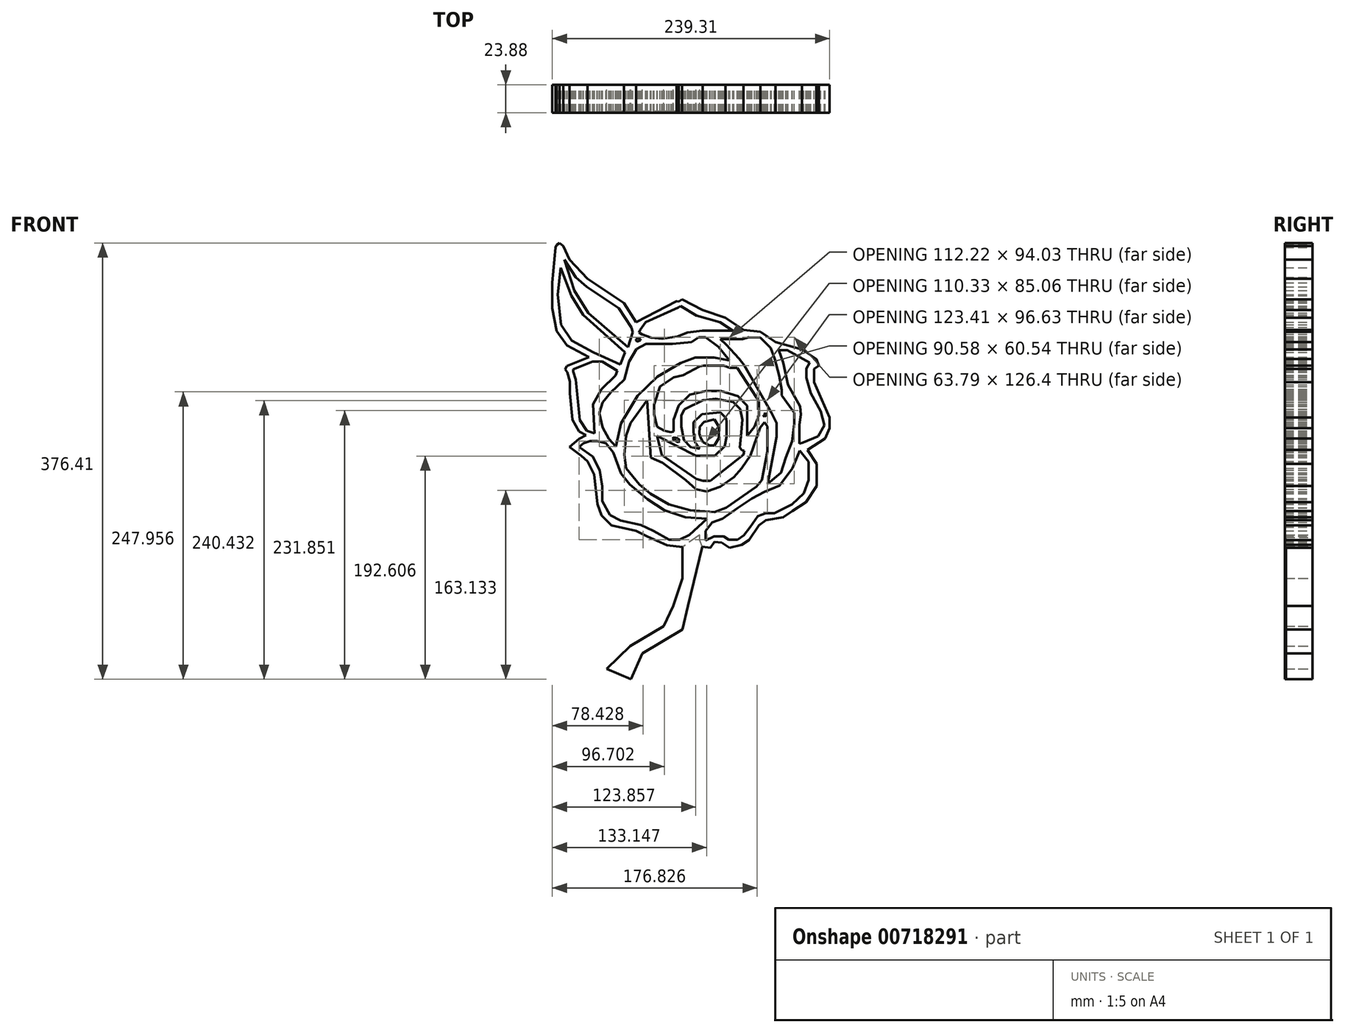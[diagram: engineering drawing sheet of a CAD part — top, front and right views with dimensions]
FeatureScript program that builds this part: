
annotation { "Feature Type Name" : "Feature", "Feature Type Description" : "" }
export const myFeature = defineFeature(function(context is Context, id is Id, definition is map)
    precondition{}
    {
        {
            var Q0;
            Q0=qCreatedBy(makeId("Front.planeOp"),FACE);
            var sketch = newSketch(context, id + "F0", { "sketchPlane" : qUnion([Q0])});
            skLineSegment(sketch, "E0", {"start": v(-232.05, 241.43) * mm, "end": v(-222.86, 217.3) * mm});
            skLineSegment(sketch, "E1", {"start": v(-222.86, 217.3) * mm, "end": v(-212.75, 200.98) * mm});
            skLineSegment(sketch, "E2", {"start": v(-212.75, 200.98) * mm, "end": v(-176.66, 168.58) * mm});
            skLineSegment(sketch, "E3", {"start": v(-176.66, 168.58) * mm, "end": v(-180.8, 158) * mm});
            skLineSegment(sketch, "E4", {"start": v(-180.8, 158) * mm, "end": v(-203.78, 168.58) * mm});
            skLineSegment(sketch, "E5", {"start": v(-203.78, 168.58) * mm, "end": v(-222.4, 178.69) * mm});
            skLineSegment(sketch, "E6", {"start": v(-222.4, 178.69) * mm, "end": v(-231.82, 192.25) * mm});
            skLineSegment(sketch, "E7", {"start": v(-231.82, 192.25) * mm, "end": v(-234.58, 218.45) * mm});
            skLineSegment(sketch, "E8", {"start": v(-234.58, 218.45) * mm, "end": v(-232.05, 241.43) * mm});
            skLineSegment(sketch, "E9", {"start": v(-228.84, 248.56) * mm, "end": v(-220.33, 221.67) * mm});
            skLineSegment(sketch, "E10", {"start": v(-220.33, 221.67) * mm, "end": v(-208.38, 202.36) * mm});
            skLineSegment(sketch, "E11", {"start": v(-208.38, 202.36) * mm, "end": v(-173.9, 172.94) * mm});
            skLineSegment(sketch, "E12", {"start": v(-173.9, 172.94) * mm, "end": v(-169.76, 185.81) * mm});
            skLineSegment(sketch, "E13", {"start": v(-169.76, 185.81) * mm, "end": v(-171.27, 190.12) * mm});
            skLineSegment(sketch, "E14", {"start": v(-171.27, 190.12) * mm, "end": v(-181.94, 206.5) * mm});
            skLineSegment(sketch, "E15", {"start": v(-181.94, 206.5) * mm, "end": v(-209.53, 225.11) * mm});
            skLineSegment(sketch, "E16", {"start": v(-209.53, 225.11) * mm, "end": v(-218.95, 233.39) * mm});
            skLineSegment(sketch, "E17", {"start": v(-218.95, 233.39) * mm, "end": v(-228.84, 248.56) * mm});
            skLineSegment(sketch, "E18", {"start": v(-221.16, 152) * mm, "end": v(-218.95, 145.01) * mm});
            skLineSegment(sketch, "E19", {"start": v(-218.95, 145.01) * mm, "end": v(-215.7, 110.18) * mm});
            skLineSegment(sketch, "E20", {"start": v(-215.7, 110.18) * mm, "end": v(-209.53, 100.89) * mm});
            skLineSegment(sketch, "E21", {"start": v(-209.53, 100.89) * mm, "end": v(-202.83, 98.73) * mm});
            skLineSegment(sketch, "E22", {"start": v(-202.83, 98.73) * mm, "end": v(-204.08, 123.8) * mm});
            skLineSegment(sketch, "E23", {"start": v(-204.08, 123.8) * mm, "end": v(-196.82, 136.67) * mm});
            skLineSegment(sketch, "E24", {"start": v(-196.82, 136.67) * mm, "end": v(-184.67, 148.4) * mm});
            skLineSegment(sketch, "E25", {"start": v(-184.67, 148.4) * mm, "end": v(-183.31, 152.6) * mm});
            skLineSegment(sketch, "E26", {"start": v(-183.31, 152.6) * mm, "end": v(-196.1, 160.52) * mm});
            skLineSegment(sketch, "E27", {"start": v(-196.1, 160.52) * mm, "end": v(-204.61, 160.52) * mm});
            skLineSegment(sketch, "E28", {"start": v(-204.61, 160.52) * mm, "end": v(-221.16, 153.85) * mm});
            skLineSegment(sketch, "E29", {"start": v(-221.16, 153.85) * mm, "end": v(-221.16, 152) * mm});
            skLineSegment(sketch, "E30", {"start": v(-166.75, 171.42) * mm, "end": v(-172.92, 160.37) * mm});
            skLineSegment(sketch, "E31", {"start": v(-172.92, 160.37) * mm, "end": v(-177.15, 145.01) * mm});
            skLineSegment(sketch, "E32", {"start": v(-177.15, 145.01) * mm, "end": v(-188.85, 133.72) * mm});
            skLineSegment(sketch, "E33", {"start": v(-188.85, 133.72) * mm, "end": v(-196, 125.27) * mm});
            skLineSegment(sketch, "E34", {"start": v(-196, 125.27) * mm, "end": v(-198.72, 115.93) * mm});
            skLineSegment(sketch, "E35", {"start": v(-198.72, 115.93) * mm, "end": v(-195.82, 103.76) * mm});
            skLineSegment(sketch, "E36", {"start": v(-195.82, 103.76) * mm, "end": v(-190.6, 93.7) * mm});
            skLineSegment(sketch, "E37", {"start": v(-190.6, 93.7) * mm, "end": v(-187.1, 90.09) * mm});
            skLineSegment(sketch, "E38", {"start": v(-187.1, 90.09) * mm, "end": v(-184.44, 87.32) * mm});
            skLineSegment(sketch, "E39", {"start": v(-184.44, 87.32) * mm, "end": v(-179.97, 107.04) * mm});
            skLineSegment(sketch, "E40", {"start": v(-179.97, 107.04) * mm, "end": v(-165.86, 131) * mm});
            skLineSegment(sketch, "E41", {"start": v(-165.86, 131) * mm, "end": v(-148.63, 147.63) * mm});
            skLineSegment(sketch, "E42", {"start": v(-148.63, 147.63) * mm, "end": v(-128.71, 159.28) * mm});
            skLineSegment(sketch, "E43", {"start": v(-128.71, 159.28) * mm, "end": v(-115.83, 164.1) * mm});
            skLineSegment(sketch, "E44", {"start": v(-115.83, 164.1) * mm, "end": v(-99.62, 164.1) * mm});
            skLineSegment(sketch, "E45", {"start": v(-99.62, 164.1) * mm, "end": v(-86.5, 161.36) * mm});
            skLineSegment(sketch, "E46", {"start": v(-86.5, 161.36) * mm, "end": v(-95.92, 173.3) * mm});
            skLineSegment(sketch, "E47", {"start": v(-95.92, 173.3) * mm, "end": v(-106.96, 181.35) * mm});
            skLineSegment(sketch, "E48", {"start": v(-106.96, 181.35) * mm, "end": v(-112.93, 181.35) * mm});
            skLineSegment(sketch, "E49", {"start": v(-112.93, 181.35) * mm, "end": v(-119.14, 177.44) * mm});
            skLineSegment(sketch, "E50", {"start": v(-119.14, 177.44) * mm, "end": v(-135.69, 175.6) * mm});
            skLineSegment(sketch, "E51", {"start": v(-135.69, 175.6) * mm, "end": v(-158.45, 175.6) * mm});
            skLineSegment(sketch, "E52", {"start": v(-158.45, 175.6) * mm, "end": v(-166.75, 171.42) * mm});
            skLineSegment(sketch, "E53", {"start": v(-216.05, 86.96) * mm, "end": v(-204.56, 78.46) * mm});
            skLineSegment(sketch, "E54", {"start": v(-204.56, 78.46) * mm, "end": v(-198.35, 66.97) * mm});
            skLineSegment(sketch, "E55", {"start": v(-198.35, 66.97) * mm, "end": v(-196.05, 52.95) * mm});
            skLineSegment(sketch, "E56", {"start": v(-196.05, 52.95) * mm, "end": v(-196.05, 40.3) * mm});
            skLineSegment(sketch, "E57", {"start": v(-196.05, 40.3) * mm, "end": v(-189.62, 28.12) * mm});
            skLineSegment(sketch, "E58", {"start": v(-189.62, 28.12) * mm, "end": v(-180.42, 23.3) * mm});
            skLineSegment(sketch, "E59", {"start": v(-180.42, 23.3) * mm, "end": v(-162.95, 19.62) * mm});
            skLineSegment(sketch, "E60", {"start": v(-162.95, 19.62) * mm, "end": v(-152.15, 14.34) * mm});
            skLineSegment(sketch, "E61", {"start": v(-152.15, 14.34) * mm, "end": v(-138.36, 6.98) * mm});
            skLineSegment(sketch, "E62", {"start": v(-138.36, 6.98) * mm, "end": v(-129.4, 6.98) * mm});
            skLineSegment(sketch, "E63", {"start": v(-129.4, 6.98) * mm, "end": v(-120.89, 10.89) * mm});
            skLineSegment(sketch, "E64", {"start": v(-120.89, 10.89) * mm, "end": v(-105.71, 24.9) * mm});
            skLineSegment(sketch, "E65", {"start": v(-105.71, 24.9) * mm, "end": v(-124.4, 26.23) * mm});
            skLineSegment(sketch, "E66", {"start": v(-124.4, 26.23) * mm, "end": v(-142.6, 32.4) * mm});
            skLineSegment(sketch, "E67", {"start": v(-142.6, 32.4) * mm, "end": v(-157.24, 41.83) * mm});
            skLineSegment(sketch, "E68", {"start": v(-157.24, 41.83) * mm, "end": v(-172.35, 54.5) * mm});
            skLineSegment(sketch, "E69", {"start": v(-172.35, 54.5) * mm, "end": v(-180, 64.1) * mm});
            skLineSegment(sketch, "E70", {"start": v(-180, 64.1) * mm, "end": v(-186.66, 81.97) * mm});
            skLineSegment(sketch, "E71", {"start": v(-186.66, 81.97) * mm, "end": v(-193.16, 90.1) * mm});
            skLineSegment(sketch, "E72", {"start": v(-193.16, 90.1) * mm, "end": v(-200.63, 92.04) * mm});
            skLineSegment(sketch, "E73", {"start": v(-200.63, 92.04) * mm, "end": v(-206.65, 92.04) * mm});
            skLineSegment(sketch, "E74", {"start": v(-206.65, 92.04) * mm, "end": v(-212.34, 90.1) * mm});
            skLineSegment(sketch, "E75", {"start": v(-212.34, 90.1) * mm, "end": v(-216.05, 86.96) * mm});
            skLineSegment(sketch, "E76", {"start": v(-163.4, 187.7) * mm, "end": v(-158.81, 194.5) * mm});
            skLineSegment(sketch, "E77", {"start": v(-158.81, 194.5) * mm, "end": v(-130.56, 207.21) * mm});
            skLineSegment(sketch, "E78", {"start": v(-130.56, 207.21) * mm, "end": v(-128.72, 208.41) * mm});
            skLineSegment(sketch, "E79", {"start": v(-128.72, 208.41) * mm, "end": v(-114.94, 200.32) * mm});
            skLineSegment(sketch, "E80", {"start": v(-114.94, 200.32) * mm, "end": v(-94.45, 194.62) * mm});
            skLineSegment(sketch, "E81", {"start": v(-94.45, 194.62) * mm, "end": v(-83.52, 187.24) * mm});
            skLineSegment(sketch, "E82", {"start": v(-83.52, 187.24) * mm, "end": v(-88.47, 187.24) * mm});
            skLineSegment(sketch, "E83", {"start": v(-88.47, 187.24) * mm, "end": v(-109.85, 187.24) * mm});
            skLineSegment(sketch, "E84", {"start": v(-109.85, 187.24) * mm, "end": v(-122.51, 185.5) * mm});
            skLineSegment(sketch, "E85", {"start": v(-122.51, 185.5) * mm, "end": v(-131.4, 182.08) * mm});
            skLineSegment(sketch, "E86", {"start": v(-131.4, 182.08) * mm, "end": v(-144.44, 180.23) * mm});
            skLineSegment(sketch, "E87", {"start": v(-144.44, 180.23) * mm, "end": v(-154.1, 181.3) * mm});
            skLineSegment(sketch, "E88", {"start": v(-154.1, 181.3) * mm, "end": v(-161.93, 184) * mm});
            skLineSegment(sketch, "E89", {"start": v(-161.93, 184) * mm, "end": v(-164.44, 185.7) * mm});
            skLineSegment(sketch, "E90", {"start": v(-164.44, 185.7) * mm, "end": v(-163.4, 187.7) * mm});
            skLineSegment(sketch, "E91", {"start": v(-94.38, 179.88) * mm, "end": v(-75.05, 179.88) * mm});
            skLineSegment(sketch, "E92", {"start": v(-75.05, 179.88) * mm, "end": v(-69.83, 181.43) * mm});
            skLineSegment(sketch, "E93", {"start": v(-69.83, 181.43) * mm, "end": v(-59.58, 181.04) * mm});
            skLineSegment(sketch, "E94", {"start": v(-59.58, 181.04) * mm, "end": v(-50.89, 172.15) * mm});
            skLineSegment(sketch, "E95", {"start": v(-50.89, 172.15) * mm, "end": v(-47.4, 162.88) * mm});
            skLineSegment(sketch, "E96", {"start": v(-47.4, 162.88) * mm, "end": v(-43.35, 148.58) * mm});
            skLineSegment(sketch, "E97", {"start": v(-43.35, 148.58) * mm, "end": v(-41.22, 136.01) * mm});
            skLineSegment(sketch, "E98", {"start": v(-41.22, 136.01) * mm, "end": v(-41.22, 131.38) * mm});
            skLineSegment(sketch, "E99", {"start": v(-41.22, 131.38) * mm, "end": v(-30.6, 116.5) * mm});
            skLineSegment(sketch, "E100", {"start": v(-30.6, 116.5) * mm, "end": v(-30.6, 106.78) * mm});
            skLineSegment(sketch, "E101", {"start": v(-30.6, 106.78) * mm, "end": v(-32.47, 91.61) * mm});
            skLineSegment(sketch, "E102", {"start": v(-32.47, 91.61) * mm, "end": v(-37.66, 77.8) * mm});
            skLineSegment(sketch, "E103", {"start": v(-37.66, 77.8) * mm, "end": v(-41.99, 64.72) * mm});
            skLineSegment(sketch, "E104", {"start": v(-41.99, 64.72) * mm, "end": v(-53.2, 55.03) * mm});
            skLineSegment(sketch, "E105", {"start": v(-53.2, 55.03) * mm, "end": v(-45.57, 95.66) * mm});
            skLineSegment(sketch, "E106", {"start": v(-45.57, 95.66) * mm, "end": v(-45.57, 107.52) * mm});
            skLineSegment(sketch, "E107", {"start": v(-45.57, 107.52) * mm, "end": v(-50.12, 116.5) * mm});
            skLineSegment(sketch, "E108", {"start": v(-50.12, 116.5) * mm, "end": v(-73.68, 157.41) * mm});
            skLineSegment(sketch, "E109", {"start": v(-73.68, 157.41) * mm, "end": v(-78.17, 163.1) * mm});
            skLineSegment(sketch, "E110", {"start": v(-78.17, 163.1) * mm, "end": v(-89.3, 175) * mm});
            skLineSegment(sketch, "E111", {"start": v(-89.3, 175) * mm, "end": v(-94.38, 179.88) * mm});
            skLineSegment(sketch, "E112", {"start": v(-157.5, 127.3) * mm, "end": v(-171.82, 107.52) * mm});
            skLineSegment(sketch, "E113", {"start": v(-171.82, 107.52) * mm, "end": v(-175.65, 96.81) * mm});
            skLineSegment(sketch, "E114", {"start": v(-175.65, 96.81) * mm, "end": v(-177.16, 80.3) * mm});
            skLineSegment(sketch, "E115", {"start": v(-177.16, 80.3) * mm, "end": v(-175.65, 68.32) * mm});
            skLineSegment(sketch, "E116", {"start": v(-175.65, 68.32) * mm, "end": v(-164.1, 54.62) * mm});
            skLineSegment(sketch, "E117", {"start": v(-164.1, 54.62) * mm, "end": v(-154.46, 46.55) * mm});
            skLineSegment(sketch, "E118", {"start": v(-154.46, 46.55) * mm, "end": v(-138.8, 37.32) * mm});
            skLineSegment(sketch, "E119", {"start": v(-138.8, 37.32) * mm, "end": v(-120.4, 32.22) * mm});
            skLineSegment(sketch, "E120", {"start": v(-120.4, 32.22) * mm, "end": v(-99.3, 30.67) * mm});
            skLineSegment(sketch, "E121", {"start": v(-99.3, 30.67) * mm, "end": v(-89.3, 34.44) * mm});
            skLineSegment(sketch, "E122", {"start": v(-89.3, 34.44) * mm, "end": v(-63.17, 52.6) * mm});
            skLineSegment(sketch, "E123", {"start": v(-63.17, 52.6) * mm, "end": v(-58.4, 58.3) * mm});
            skLineSegment(sketch, "E124", {"start": v(-58.4, 58.3) * mm, "end": v(-53.75, 83.02) * mm});
            skLineSegment(sketch, "E125", {"start": v(-53.75, 83.02) * mm, "end": v(-53.75, 104.5) * mm});
            skLineSegment(sketch, "E126", {"start": v(-53.75, 104.5) * mm, "end": v(-55.51, 107.04) * mm});
            skLineSegment(sketch, "E127", {"start": v(-55.51, 107.04) * mm, "end": v(-56.2, 108.02) * mm});
            skLineSegment(sketch, "E128", {"start": v(-56.2, 108.02) * mm, "end": v(-59.88, 103.36) * mm});
            skLineSegment(sketch, "E129", {"start": v(-59.88, 103.36) * mm, "end": v(-68.22, 79.47) * mm});
            skLineSegment(sketch, "E130", {"start": v(-68.22, 79.47) * mm, "end": v(-75.9, 68.54) * mm});
            skLineSegment(sketch, "E131", {"start": v(-75.9, 68.54) * mm, "end": v(-82.4, 60.86) * mm});
            skLineSegment(sketch, "E132", {"start": v(-82.4, 60.86) * mm, "end": v(-94.27, 52.6) * mm});
            skLineSegment(sketch, "E133", {"start": v(-94.27, 52.6) * mm, "end": v(-106.03, 48.46) * mm});
            skLineSegment(sketch, "E134", {"start": v(-106.03, 48.46) * mm, "end": v(-115.37, 50.21) * mm});
            skLineSegment(sketch, "E135", {"start": v(-115.37, 50.21) * mm, "end": v(-124.05, 58.3) * mm});
            skLineSegment(sketch, "E136", {"start": v(-124.05, 58.3) * mm, "end": v(-144.13, 73.27) * mm});
            skLineSegment(sketch, "E137", {"start": v(-144.13, 73.27) * mm, "end": v(-154.17, 77.7) * mm});
            skLineSegment(sketch, "E138", {"start": v(-154.17, 77.7) * mm, "end": v(-157.5, 127.3) * mm});
            skLineSegment(sketch, "E139", {"start": v(-149, 96.54) * mm, "end": v(-115.36, 79.15) * mm});
            skLineSegment(sketch, "E140", {"start": v(-115.36, 79.15) * mm, "end": v(-99.11, 79.15) * mm});
            skLineSegment(sketch, "E141", {"start": v(-99.11, 79.15) * mm, "end": v(-90.55, 87.42) * mm});
            skLineSegment(sketch, "E142", {"start": v(-90.55, 87.42) * mm, "end": v(-88.96, 95.87) * mm});
            skLineSegment(sketch, "E143", {"start": v(-88.96, 95.87) * mm, "end": v(-88.96, 108.02) * mm});
            skLineSegment(sketch, "E144", {"start": v(-88.96, 108.02) * mm, "end": v(-89.34, 111.66) * mm});
            skLineSegment(sketch, "E145", {"start": v(-89.34, 111.66) * mm, "end": v(-94.28, 116.77) * mm});
            skLineSegment(sketch, "E146", {"start": v(-94.28, 116.77) * mm, "end": v(-110.01, 115.11) * mm});
            skLineSegment(sketch, "E147", {"start": v(-110.01, 115.11) * mm, "end": v(-117.36, 108.02) * mm});
            skLineSegment(sketch, "E148", {"start": v(-117.36, 108.02) * mm, "end": v(-117.36, 100.19) * mm});
            skLineSegment(sketch, "E149", {"start": v(-117.36, 100.19) * mm, "end": v(-116.45, 91.6) * mm});
            skLineSegment(sketch, "E150", {"start": v(-116.45, 91.6) * mm, "end": v(-112.11, 85.36) * mm});
            skLineSegment(sketch, "E151", {"start": v(-112.11, 85.36) * mm, "end": v(-119.91, 86.83) * mm});
            skLineSegment(sketch, "E152", {"start": v(-119.91, 86.83) * mm, "end": v(-125.72, 92.85) * mm});
            skLineSegment(sketch, "E153", {"start": v(-125.72, 92.85) * mm, "end": v(-127.96, 104.4) * mm});
            skLineSegment(sketch, "E154", {"start": v(-127.96, 104.4) * mm, "end": v(-127.96, 113.98) * mm});
            skLineSegment(sketch, "E155", {"start": v(-127.96, 113.98) * mm, "end": v(-125.34, 119.11) * mm});
            skLineSegment(sketch, "E156", {"start": v(-125.34, 119.11) * mm, "end": v(-109.15, 127.3) * mm});
            skLineSegment(sketch, "E157", {"start": v(-109.15, 127.3) * mm, "end": v(-98.4, 128.43) * mm});
            skLineSegment(sketch, "E158", {"start": v(-98.4, 128.43) * mm, "end": v(-90.53, 126.95) * mm});
            skLineSegment(sketch, "E159", {"start": v(-90.53, 126.95) * mm, "end": v(-83.02, 125.54) * mm});
            skLineSegment(sketch, "E160", {"start": v(-83.02, 125.54) * mm, "end": v(-77.24, 119.55) * mm});
            skLineSegment(sketch, "E161", {"start": v(-77.24, 119.55) * mm, "end": v(-75.18, 110.45) * mm});
            skLineSegment(sketch, "E162", {"start": v(-75.18, 110.45) * mm, "end": v(-76.55, 96.08) * mm});
            skLineSegment(sketch, "E163", {"start": v(-76.55, 96.08) * mm, "end": v(-77.6, 86.16) * mm});
            skLineSegment(sketch, "E164", {"start": v(-77.6, 86.16) * mm, "end": v(-75.56, 84.05) * mm});
            skLineSegment(sketch, "E165", {"start": v(-75.56, 84.05) * mm, "end": v(-73.74, 83.7) * mm});
            skLineSegment(sketch, "E166", {"start": v(-73.74, 83.7) * mm, "end": v(-74.39, 80.29) * mm});
            skLineSegment(sketch, "E167", {"start": v(-74.39, 80.29) * mm, "end": v(-102.9, 57.7) * mm});
            skLineSegment(sketch, "E168", {"start": v(-102.9, 57.7) * mm, "end": v(-109.24, 57.7) * mm});
            skLineSegment(sketch, "E169", {"start": v(-109.24, 57.7) * mm, "end": v(-115, 59.28) * mm});
            skLineSegment(sketch, "E170", {"start": v(-115, 59.28) * mm, "end": v(-144.74, 79.9) * mm});
            skLineSegment(sketch, "E171", {"start": v(-144.74, 79.9) * mm, "end": v(-149, 96.54) * mm});
            skLineSegment(sketch, "E172", {"start": v(-70.97, 96.54) * mm, "end": v(-70.97, 122.54) * mm});
            skPoint(sketch, "E172.endSnap0", {"position": v(-80.13, 122.54) * mm});
            skLineSegment(sketch, "E173", {"start": v(-70.97, 122.54) * mm, "end": v(-78.94, 130.8) * mm});
            skLineSegment(sketch, "E174", {"start": v(-78.94, 130.8) * mm, "end": v(-93.58, 135.23) * mm});
            skLineSegment(sketch, "E175", {"start": v(-93.58, 135.23) * mm, "end": v(-106.66, 135.23) * mm});
            skLineSegment(sketch, "E176", {"start": v(-106.66, 135.23) * mm, "end": v(-120.6, 132.07) * mm});
            skLineSegment(sketch, "E177", {"start": v(-120.6, 132.07) * mm, "end": v(-130.28, 122.73) * mm});
            skLineSegment(sketch, "E178", {"start": v(-130.28, 122.73) * mm, "end": v(-134.62, 110.45) * mm});
            skLineSegment(sketch, "E179", {"start": v(-134.62, 110.45) * mm, "end": v(-134.62, 100.19) * mm});
            skLineSegment(sketch, "E180", {"start": v(-134.62, 100.19) * mm, "end": v(-136.78, 99.7) * mm});
            skLineSegment(sketch, "E181", {"start": v(-136.78, 99.7) * mm, "end": v(-142.5, 100.78) * mm});
            skLineSegment(sketch, "E182", {"start": v(-142.5, 100.78) * mm, "end": v(-149, 104.4) * mm});
            skLineSegment(sketch, "E183", {"start": v(-149, 104.4) * mm, "end": v(-150.37, 110.45) * mm});
            skLineSegment(sketch, "E184", {"start": v(-150.37, 110.45) * mm, "end": v(-151.45, 115.23) * mm});
            skLineSegment(sketch, "E185", {"start": v(-151.45, 115.23) * mm, "end": v(-151.45, 123.33) * mm});
            skLineSegment(sketch, "E186", {"start": v(-151.45, 123.33) * mm, "end": v(-146.32, 139) * mm});
            skLineSegment(sketch, "E187", {"start": v(-146.32, 139) * mm, "end": v(-134.62, 146.93) * mm});
            skLineSegment(sketch, "E188", {"start": v(-134.62, 146.93) * mm, "end": v(-126.4, 148.8) * mm});
            skLineSegment(sketch, "E189", {"start": v(-126.4, 148.8) * mm, "end": v(-112.11, 156.25) * mm});
            skLineSegment(sketch, "E190", {"start": v(-112.11, 156.25) * mm, "end": v(-108.42, 157.08) * mm});
            skLineSegment(sketch, "E191", {"start": v(-108.42, 157.08) * mm, "end": v(-91.54, 157.08) * mm});
            skLineSegment(sketch, "E192", {"start": v(-91.54, 157.08) * mm, "end": v(-86.18, 155.27) * mm});
            skLineSegment(sketch, "E193", {"start": v(-86.18, 155.27) * mm, "end": v(-79.54, 155.27) * mm});
            skLineSegment(sketch, "E194", {"start": v(-79.54, 155.27) * mm, "end": v(-63.27, 129.7) * mm});
            skLineSegment(sketch, "E195", {"start": v(-63.27, 129.7) * mm, "end": v(-60.88, 125.54) * mm});
            skLineSegment(sketch, "E196", {"start": v(-60.88, 125.54) * mm, "end": v(-60.88, 114.1) * mm});
            skLineSegment(sketch, "E197", {"start": v(-60.88, 114.1) * mm, "end": v(-64.81, 104.4) * mm});
            skLineSegment(sketch, "E198", {"start": v(-64.81, 104.4) * mm, "end": v(-70.97, 96.54) * mm});
            skLineSegment(sketch, "E199", {"start": v(-106.9, 6.08) * mm, "end": v(-106.9, 14.36) * mm});
            skLineSegment(sketch, "E200", {"start": v(-106.9, 14.36) * mm, "end": v(-101.22, 21.7) * mm});
            skLineSegment(sketch, "E201", {"start": v(-101.22, 21.7) * mm, "end": v(-92.23, 25) * mm});
            skLineSegment(sketch, "E202", {"start": v(-92.23, 25) * mm, "end": v(-79.22, 34.24) * mm});
            skLineSegment(sketch, "E203", {"start": v(-79.22, 34.24) * mm, "end": v(-66.91, 42.52) * mm});
            skLineSegment(sketch, "E204", {"start": v(-66.91, 42.52) * mm, "end": v(-56.27, 48.2) * mm});
            skLineSegment(sketch, "E205", {"start": v(-56.27, 48.2) * mm, "end": v(-43.25, 53.64) * mm});
            skLineSegment(sketch, "E206", {"start": v(-43.25, 53.64) * mm, "end": v(-32.13, 68.3) * mm});
            skLineSegment(sketch, "E207", {"start": v(-32.13, 68.3) * mm, "end": v(-25.75, 83.69) * mm});
            skLineSegment(sketch, "E208", {"start": v(-25.75, 83.69) * mm, "end": v(-17.94, 74.22) * mm});
            skLineSegment(sketch, "E209", {"start": v(-17.94, 74.22) * mm, "end": v(-17.94, 58.37) * mm});
            skLineSegment(sketch, "E210", {"start": v(-17.94, 58.37) * mm, "end": v(-22.2, 46.78) * mm});
            skLineSegment(sketch, "E211", {"start": v(-22.2, 46.78) * mm, "end": v(-32.37, 37.31) * mm});
            skLineSegment(sketch, "E212", {"start": v(-32.37, 37.31) * mm, "end": v(-47.51, 29.74) * mm});
            skLineSegment(sketch, "E213", {"start": v(-47.51, 29.74) * mm, "end": v(-54.85, 29.74) * mm});
            skLineSegment(sketch, "E214", {"start": v(-54.85, 29.74) * mm, "end": v(-62.03, 27.06) * mm});
            skLineSegment(sketch, "E215", {"start": v(-62.03, 27.06) * mm, "end": v(-68.57, 17.67) * mm});
            skLineSegment(sketch, "E216", {"start": v(-68.57, 17.67) * mm, "end": v(-74.01, 10.58) * mm});
            skLineSegment(sketch, "E217", {"start": v(-74.01, 10.58) * mm, "end": v(-79.23, 6.95) * mm});
            skLineSegment(sketch, "E218", {"start": v(-79.23, 6.95) * mm, "end": v(-87.02, 6.95) * mm});
            skLineSegment(sketch, "E219", {"start": v(-87.02, 6.95) * mm, "end": v(-91.28, 9.87) * mm});
            skLineSegment(sketch, "E220", {"start": v(-91.28, 9.87) * mm, "end": v(-99.8, 9.87) * mm});
            skLineSegment(sketch, "E221", {"start": v(-99.8, 9.87) * mm, "end": v(-106.9, 6.08) * mm});
            skLineSegment(sketch, "E222", {"start": v(-43.77, 170.32) * mm, "end": v(-36.48, 170.32) * mm});
            skLineSegment(sketch, "E223", {"start": v(-36.48, 170.32) * mm, "end": v(-17.03, 159.72) * mm});
            skLineSegment(sketch, "E224", {"start": v(-17.03, 159.72) * mm, "end": v(-19.86, 154.53) * mm});
            skLineSegment(sketch, "E225", {"start": v(-19.86, 154.53) * mm, "end": v(-19.86, 146.46) * mm});
            skLineSegment(sketch, "E226", {"start": v(-19.86, 146.46) * mm, "end": v(-16.08, 133.13) * mm});
            skLineSegment(sketch, "E227", {"start": v(-16.08, 133.13) * mm, "end": v(-7.75, 117.51) * mm});
            skLineSegment(sketch, "E228", {"start": v(-7.75, 117.51) * mm, "end": v(-4.4, 105.75) * mm});
            skLineSegment(sketch, "E229", {"start": v(-4.4, 105.75) * mm, "end": v(-9.96, 96.08) * mm});
            skLineSegment(sketch, "E230", {"start": v(-9.96, 96.08) * mm, "end": v(-22.78, 90.56) * mm});
            skLineSegment(sketch, "E231", {"start": v(-22.78, 90.56) * mm, "end": v(-26.14, 89.6) * mm});
            skLineSegment(sketch, "E232", {"start": v(-26.14, 89.6) * mm, "end": v(-26.14, 98.82) * mm});
            skLineSegment(sketch, "E233", {"start": v(-26.14, 98.82) * mm, "end": v(-26.14, 106.02) * mm});
            skLineSegment(sketch, "E234", {"start": v(-26.14, 106.02) * mm, "end": v(-24.69, 114.89) * mm});
            skLineSegment(sketch, "E235", {"start": v(-24.69, 114.89) * mm, "end": v(-25.28, 121.93) * mm});
            skLineSegment(sketch, "E236", {"start": v(-25.28, 121.93) * mm, "end": v(-32.79, 134.97) * mm});
            skLineSegment(sketch, "E237", {"start": v(-32.79, 134.97) * mm, "end": v(-36.01, 140.57) * mm});
            skLineSegment(sketch, "E238", {"start": v(-36.01, 140.57) * mm, "end": v(-39.83, 159.72) * mm});
            skLineSegment(sketch, "E239", {"start": v(-39.83, 159.72) * mm, "end": v(-43.77, 170.32) * mm});
            skLineSegment(sketch, "E240", {"start": v(-112.13, 104.4) * mm, "end": v(-108.17, 108.44) * mm});
            skLineSegment(sketch, "E241", {"start": v(-108.17, 108.44) * mm, "end": v(-99.29, 110.71) * mm});
            skLineSegment(sketch, "E242", {"start": v(-99.29, 110.71) * mm, "end": v(-95.65, 104.4) * mm});
            skLineSegment(sketch, "E243", {"start": v(-95.65, 104.4) * mm, "end": v(-95.65, 94.46) * mm});
            skLineSegment(sketch, "E244", {"start": v(-95.65, 94.46) * mm, "end": v(-99.45, 88.04) * mm});
            skLineSegment(sketch, "E245", {"start": v(-99.45, 88.04) * mm, "end": v(-103.4, 88.04) * mm});
            skLineSegment(sketch, "E246", {"start": v(-103.4, 88.04) * mm, "end": v(-109.16, 90.84) * mm});
            skLineSegment(sketch, "E247", {"start": v(-109.16, 90.84) * mm, "end": v(-111.2, 94.37) * mm});
            skLineSegment(sketch, "E248", {"start": v(-111.2, 94.37) * mm, "end": v(-112.22, 98.37) * mm});
            skLineSegment(sketch, "E249", {"start": v(-112.22, 98.37) * mm, "end": v(-112.13, 104.4) * mm});
            skLineSegment(sketch, "E250", {"start": v(-56.19, 113.04) * mm, "end": v(-54.19, 114.2) * mm});
            skLineSegment(sketch, "E251", {"start": v(-54.19, 114.2) * mm, "end": v(-55.51, 116.5) * mm});
            skLineSegment(sketch, "E252", {"start": v(-55.51, 116.5) * mm, "end": v(-56.19, 114.17) * mm});
            skLineSegment(sketch, "E253", {"start": v(-56.19, 114.17) * mm, "end": v(-57.08, 114.17) * mm});
            skLineSegment(sketch, "E254", {"start": v(-57.08, 113.87) * mm, "end": v(-56.19, 113.04) * mm});
            skLineSegment(sketch, "E255", {"start": v(-57.08, 113.87) * mm, "end": v(-57.08, 114.17) * mm});
            skLineSegment(sketch, "E256", {"start": v(-135.47, 94) * mm, "end": v(-131.25, 91.15) * mm});
            skLineSegment(sketch, "E257", {"start": v(-131.25, 91.15) * mm, "end": v(-130.19, 91.05) * mm});
            skLineSegment(sketch, "E258", {"start": v(-130.19, 91.05) * mm, "end": v(-129.62, 92.04) * mm});
            skLineSegment(sketch, "E259", {"start": v(-129.62, 92.04) * mm, "end": v(-130.47, 93.5) * mm});
            skLineSegment(sketch, "E260", {"start": v(-130.47, 93.5) * mm, "end": v(-130.75, 94.59) * mm});
            skLineSegment(sketch, "E261", {"start": v(-130.75, 94.59) * mm, "end": v(-134.62, 94.96) * mm});
            skLineSegment(sketch, "E262", {"start": v(-134.62, 94.96) * mm, "end": v(-135.47, 94) * mm});
            skLineSegment(sketch, "E263", {"start": v(-224.61, 86.96) * mm, "end": v(-216.05, 93.7) * mm});
            skLineSegment(sketch, "E264", {"start": v(-216.05, 93.7) * mm, "end": v(-210.13, 97.12) * mm});
            skLineSegment(sketch, "E265", {"start": v(-210.13, 97.12) * mm, "end": v(-216.05, 100.18) * mm});
            skLineSegment(sketch, "E266", {"start": v(-216.05, 100.18) * mm, "end": v(-221.96, 110.45) * mm});
            skLineSegment(sketch, "E267", {"start": v(-221.96, 110.45) * mm, "end": v(-224.28, 133.11) * mm});
            skLineSegment(sketch, "E268", {"start": v(-224.28, 133.11) * mm, "end": v(-224.28, 143.4) * mm});
            skLineSegment(sketch, "E269", {"start": v(-224.28, 143.4) * mm, "end": v(-226.32, 151.38) * mm});
            skLineSegment(sketch, "E270", {"start": v(-226.32, 151.38) * mm, "end": v(-228.33, 153.81) * mm});
            skLineSegment(sketch, "E271", {"start": v(-228.33, 153.81) * mm, "end": v(-226.83, 156.72) * mm});
            skLineSegment(sketch, "E272", {"start": v(-226.83, 156.72) * mm, "end": v(-207.54, 164.48) * mm});
            skLineSegment(sketch, "E273", {"start": v(-207.54, 164.48) * mm, "end": v(-226.67, 174.37) * mm});
            skLineSegment(sketch, "E274", {"start": v(-226.67, 174.37) * mm, "end": v(-235.5, 187) * mm});
            skLineSegment(sketch, "E275", {"start": v(-235.5, 187) * mm, "end": v(-239.3, 206.68) * mm});
            skLineSegment(sketch, "E276", {"start": v(-239.3, 206.68) * mm, "end": v(-239.3, 228.35) * mm});
            skLineSegment(sketch, "E277", {"start": v(-239.3, 228.35) * mm, "end": v(-236.4, 258.84) * mm});
            skLineSegment(sketch, "E278", {"start": v(-236.4, 258.84) * mm, "end": v(-235.61, 261.14) * mm});
            skLineSegment(sketch, "E279", {"start": v(-235.61, 261.14) * mm, "end": v(-233.17, 262.8) * mm});
            skLineSegment(sketch, "E280", {"start": v(-233.17, 262.8) * mm, "end": v(-229.88, 260.22) * mm});
            skLineSegment(sketch, "E281", {"start": v(-229.88, 260.22) * mm, "end": v(-224.48, 248.58) * mm});
            skLineSegment(sketch, "E282", {"start": v(-224.48, 248.58) * mm, "end": v(-208.89, 231.98) * mm});
            skLineSegment(sketch, "E283", {"start": v(-208.89, 231.98) * mm, "end": v(-195.74, 223.1) * mm});
            skPoint(sketch, "E283.endSnap0", {"position": v(-195.74, 215.8) * mm});
            skLineSegment(sketch, "E284", {"start": v(-195.74, 223.1) * mm, "end": v(-177.6, 210.86) * mm});
            skLineSegment(sketch, "E285", {"start": v(-177.6, 210.86) * mm, "end": v(-166.93, 194.5) * mm});
            skLineSegment(sketch, "E286", {"start": v(-166.93, 194.5) * mm, "end": v(-132.03, 212.44) * mm});
            skLineSegment(sketch, "E287", {"start": v(-132.03, 212.44) * mm, "end": v(-130.23, 212.24) * mm});
            skLineSegment(sketch, "E288", {"start": v(-130.23, 212.24) * mm, "end": v(-127.45, 214.05) * mm});
            skLineSegment(sketch, "E289", {"start": v(-127.45, 214.05) * mm, "end": v(-109.67, 204.82) * mm});
            skLineSegment(sketch, "E290", {"start": v(-109.67, 204.82) * mm, "end": v(-89.76, 198.18) * mm});
            skLineSegment(sketch, "E291", {"start": v(-89.76, 198.18) * mm, "end": v(-74.4, 187.81) * mm});
            skLineSegment(sketch, "E292", {"start": v(-74.4, 187.81) * mm, "end": v(-59.6, 186.19) * mm});
            skLineSegment(sketch, "E293", {"start": v(-59.6, 186.19) * mm, "end": v(-46.53, 177.36) * mm});
            skLineSegment(sketch, "E294", {"start": v(-46.53, 177.36) * mm, "end": v(-23.65, 170.9) * mm});
            skLineSegment(sketch, "E295", {"start": v(-23.65, 170.9) * mm, "end": v(-11.44, 162.66) * mm});
            skLineSegment(sketch, "E296", {"start": v(-11.44, 162.66) * mm, "end": v(-9.25, 156.93) * mm});
            skLineSegment(sketch, "E297", {"start": v(-9.25, 156.93) * mm, "end": v(-13.26, 154.31) * mm});
            skLineSegment(sketch, "E298", {"start": v(-13.26, 154.31) * mm, "end": v(-13.26, 142.64) * mm});
            skLineSegment(sketch, "E299", {"start": v(-13.26, 142.64) * mm, "end": v(0, 112.36) * mm});
            skLineSegment(sketch, "E300", {"start": v(0, 112.36) * mm, "end": v(0, 102.92) * mm});
            skLineSegment(sketch, "E301", {"start": v(0, 102.92) * mm, "end": v(-3.86, 94.2) * mm});
            skLineSegment(sketch, "E302", {"start": v(-3.86, 94.2) * mm, "end": v(-14.15, 87.5) * mm});
            skLineSegment(sketch, "E303", {"start": v(-14.15, 87.5) * mm, "end": v(-18.94, 84.38) * mm});
            skLineSegment(sketch, "E304", {"start": v(-18.94, 84.38) * mm, "end": v(-11.02, 72.23) * mm});
            skLineSegment(sketch, "E305", {"start": v(-11.02, 72.23) * mm, "end": v(-11.02, 53.3) * mm});
            skLineSegment(sketch, "E306", {"start": v(-11.02, 53.3) * mm, "end": v(-20.44, 39.35) * mm});
            skLineSegment(sketch, "E307", {"start": v(-20.44, 39.35) * mm, "end": v(-32.19, 31.7) * mm});
            skLineSegment(sketch, "E308", {"start": v(-32.19, 31.7) * mm, "end": v(-40, 26.26) * mm});
            skLineSegment(sketch, "E309", {"start": v(-40, 26.26) * mm, "end": v(-54.85, 23.65) * mm});
            skLineSegment(sketch, "E310", {"start": v(-54.85, 23.65) * mm, "end": v(-61.07, 19.32) * mm});
            skLineSegment(sketch, "E311", {"start": v(-61.07, 19.32) * mm, "end": v(-69.6, 6.67) * mm});
            skLineSegment(sketch, "E312", {"start": v(-69.6, 6.67) * mm, "end": v(-75.9, 2.3) * mm});
            skLineSegment(sketch, "E313", {"start": v(-75.9, 2.3) * mm, "end": v(-86.47, 0) * mm});
            skLineSegment(sketch, "E314", {"start": v(-86.47, 0) * mm, "end": v(-92.88, 4.32) * mm});
            skLineSegment(sketch, "E315", {"start": v(-92.88, 4.32) * mm, "end": v(-99.35, 5.03) * mm});
            skLineSegment(sketch, "E316", {"start": v(-99.35, 5.03) * mm, "end": v(-102.75, 0) * mm});
            skLineSegment(sketch, "E317", {"start": v(-102.75, 0) * mm, "end": v(-109.95, 0.8) * mm});
            skLineSegment(sketch, "E318", {"start": v(-109.95, 0.8) * mm, "end": v(-112.19, 6.67) * mm});
            skLineSegment(sketch, "E319", {"start": v(-112.19, 6.67) * mm, "end": v(-112.19, 10.82) * mm});
            skLineSegment(sketch, "E320", {"start": v(-112.19, 10.82) * mm, "end": v(-115.1, 8.75) * mm});
            skLineSegment(sketch, "E321", {"start": v(-115.1, 8.75) * mm, "end": v(-126.94, 0.52) * mm});
            skLineSegment(sketch, "E322", {"start": v(-126.94, 0.52) * mm, "end": v(-140.24, 1.98) * mm});
            skLineSegment(sketch, "E323", {"start": v(-140.24, 1.98) * mm, "end": v(-157.33, 9.87) * mm});
            skLineSegment(sketch, "E324", {"start": v(-157.33, 9.87) * mm, "end": v(-166.93, 14.49) * mm});
            skLineSegment(sketch, "E325", {"start": v(-166.93, 14.49) * mm, "end": v(-188.39, 19.32) * mm});
            skLineSegment(sketch, "E326", {"start": v(-188.39, 19.32) * mm, "end": v(-196.95, 27.82) * mm});
            skLineSegment(sketch, "E327", {"start": v(-196.95, 27.82) * mm, "end": v(-200.44, 37.5) * mm});
            skLineSegment(sketch, "E328", {"start": v(-200.44, 37.5) * mm, "end": v(-203.3, 63.2) * mm});
            skLineSegment(sketch, "E329", {"start": v(-203.3, 63.2) * mm, "end": v(-208.85, 74.47) * mm});
            skLineSegment(sketch, "E330", {"start": v(-208.85, 74.47) * mm, "end": v(-214.45, 79.24) * mm});
            skLineSegment(sketch, "E331", {"start": v(-214.45, 79.24) * mm, "end": v(-224.61, 86.96) * mm});
            skLineSegment(sketch, "E332", {"start": v(-165.54, 177.87) * mm, "end": v(-163.17, 179.06) * mm});
            skLineSegment(sketch, "E333", {"start": v(-163.17, 179.83) * mm, "end": v(-165.77, 180.6) * mm});
            skLineSegment(sketch, "E334", {"start": v(-165.77, 180.6) * mm, "end": v(-166.97, 180.02) * mm});
            skLineSegment(sketch, "E335", {"start": v(-166.97, 180.02) * mm, "end": v(-166.9, 178.55) * mm});
            skLineSegment(sketch, "E336", {"start": v(-166.9, 178.55) * mm, "end": v(-166.48, 177.88) * mm});
            skLineSegment(sketch, "E337", {"start": v(-166.48, 177.88) * mm, "end": v(-165.54, 177.87) * mm});
            skLineSegment(sketch, "E338", {"start": v(-163.17, 179.06) * mm, "end": v(-163.17, 179.83) * mm});
            skLineSegment(sketch, "E339", {"start": v(-126.94, 0.52) * mm, "end": v(-126.94, -26.45) * mm});
            skLineSegment(sketch, "E340", {"start": v(-126.94, -26.45) * mm, "end": v(-134.79, -50.22) * mm});
            skLineSegment(sketch, "E341", {"start": v(-134.79, -50.22) * mm, "end": v(-143.28, -67.87) * mm});
            skLineSegment(sketch, "E342", {"start": v(-143.28, -67.87) * mm, "end": v(-172.04, -84.86) * mm});
            skLineSegment(sketch, "E343", {"start": v(-172.04, -84.86) * mm, "end": v(-192.3, -104.47) * mm});
            skLineSegment(sketch, "E344", {"start": v(-192.3, -104.47) * mm, "end": v(-171.38, -113.62) * mm});
            skLineSegment(sketch, "E345", {"start": v(-171.38, -113.62) * mm, "end": v(-161.57, -91.2) * mm});
            skLineSegment(sketch, "E346", {"start": v(-161.57, -91.2) * mm, "end": v(-126.94, -70.48) * mm});
            skLineSegment(sketch, "E347", {"start": v(-126.94, -70.48) * mm, "end": v(-122.37, -50.22) * mm});
            skLineSegment(sketch, "E348", {"start": v(-122.37, -50.22) * mm, "end": v(-109.95, 0.8) * mm});
            skLineSegment(sketch, "E349", {"start": v(-126.94, 0.52) * mm, "end": v(-115.1, 8.75) * mm});
            skLineSegment(sketch, "E350", {"start": v(-112.19, 10.82) * mm, "end": v(-112.19, 6.67) * mm});
            skLineSegment(sketch, "E351", {"start": v(-112.19, 6.67) * mm, "end": v(-109.95, 0.8) * mm});
            skSolve(sketch);
        }
        {
            var Q0;
            Q0=makeQuery(id+"F0.imprint","IMPRINT",FACE,{"disambiguationData":[TD([[makeQuery(id+"F0.imprint","IMPRINT",EDGE,{"derivedFrom":sQuery(id+"F0.wireOp",EDGE,"E0")}),1.0]])]});
            var Q1;
            Q1=makeQuery(id+"F0.imprint","IMPRINT",FACE,{"disambiguationData":[TD([[makeQuery(id+"F0.imprint","IMPRINT",EDGE,{"derivedFrom":sQuery(id+"F0.wireOp",EDGE,"E318")}),1.0]])]});
            extrude(context, id + "F1", {"entities" : qUnion([Q0, Q1]), "depth" : 23.88 * mm, "offsetDistance" : 25.4 * mm});
        }
        {
            var Q0;
            Q0=makeQuery(id+"F0.imprint","IMPRINT",FACE,{"disambiguationData":[TD([[makeQuery(id+"F0.imprint","IMPRINT",EDGE,{"derivedFrom":sQuery(id+"F0.wireOp",EDGE,"E339")}),1.0]])]});
            extrude(context, id + "F2", {"entities" : qUnion([Q0]), "depth" : 22.86 * mm, "offsetDistance" : 25.4 * mm});
        }
    });
